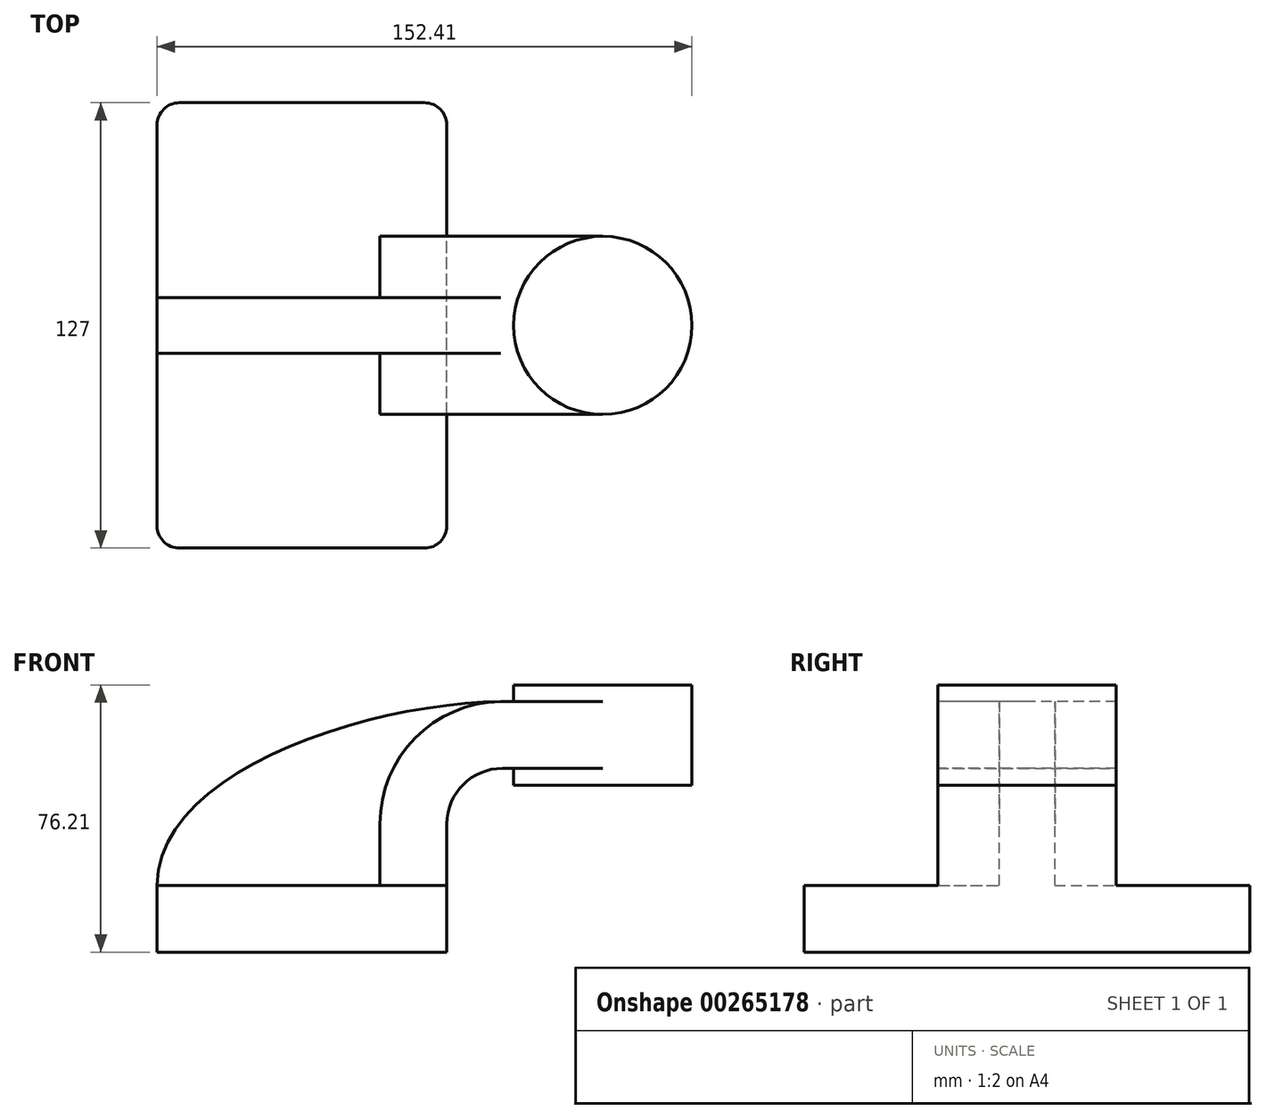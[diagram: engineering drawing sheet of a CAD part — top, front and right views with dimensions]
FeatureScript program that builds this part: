
annotation { "Feature Type Name" : "Feature", "Feature Type Description" : "" }
export const myFeature = defineFeature(function(context is Context, id is Id, definition is map)
    precondition{}
    {
        {
            var Q0;
            Q0=qCreatedBy(makeId("Front.planeOp"),FACE);
            var sketch = newSketch(context, id + "F0", { "sketchPlane" : qUnion([Q0])});
            skLineSegment(sketch, "E0.bottom", {"start": v(-41.28, 9.52) * mm, "end": v(41.28, 9.52) * mm});
            skLineSegment(sketch, "E0.top", {"start": v(-41.28, -9.53) * mm, "end": v(41.28, -9.53) * mm});
            skLineSegment(sketch, "E0.left", {"start": v(-41.28, 9.52) * mm, "end": v(-41.28, -9.53) * mm});
            skLineSegment(sketch, "E0.right", {"start": v(41.28, 9.52) * mm, "end": v(41.28, -9.53) * mm});
            skPoint(sketch, "E0.middle", {"position": v(0, 0) * mm});
            skLineSegment(sketch, "E1.bottom", {"start": v(60.33, 38.1) * mm, "end": v(111.13, 38.1) * mm});
            skLineSegment(sketch, "E1.top", {"start": v(60.33, 66.67) * mm, "end": v(111.13, 66.67) * mm});
            skLineSegment(sketch, "E1.left", {"start": v(60.33, 38.1) * mm, "end": v(60.33, 66.67) * mm});
            skLineSegment(sketch, "E1.right", {"start": v(111.13, 38.1) * mm, "end": v(111.13, 66.67) * mm});
            skPoint(sketch, "E1.middle", {"position": v(85.73, 52.39) * mm});
            skLineSegment(sketch, "E2", {"start": v(41.28, 9.52) * mm, "end": v(41.28, 27) * mm});
            skArc(sketch, "E3", {"start": v(41.28, 27) * mm, "mid": v(45.92, 38.23) * mm, "end": v(57.15, 42.88) * mm});
            skLineSegment(sketch, "E4", {"start": v(57.15, 42.88) * mm, "end": v(85.72, 42.88) * mm});
            skLineSegment(sketch, "E5.0", {"start": v(57.15, 61.93) * mm, "end": v(85.72, 61.93) * mm});
            skArc(sketch, "E5.1", {"start": v(22.23, 27) * mm, "mid": v(32.45, 51.7) * mm, "end": v(57.15, 61.93) * mm});
            skLineSegment(sketch, "E5.2", {"start": v(22.23, 9.52) * mm, "end": v(22.23, 27) * mm});
            skFitSpline(sketch, "E6", {"points": [v(-41.28, 9.53) * mm, v(57.15, 61.93) * mm], "startDerivative": vector(0.5, 99.63) * mm, "endDerivative": vector(110.98, 0.55) * mm});
            skLineSegment(sketch, "E7", {"start": v(85.73, 38.1) * mm, "end": v(85.73, 66.67) * mm});
            skSolve(sketch);
        }
        {
            var Q0;
            Q0=makeQuery(id+"F0.imprint","IMPRINT",FACE,{"disambiguationData":[TD([[makeQuery(id+"F0.imprint","IMPRINT",EDGE,{"derivedFrom":sQuery(id+"F0.wireOp",EDGE,"E0.top")}),1.0]])]});
            extrude(context, id + "F1", {"entities" : qUnion([Q0]), "endBound" : BoundingType.SYMMETRIC, "depth" : 127 * mm});
        }
        {
            var Q0;
            {var subQ0=sQuery(id+"F0.wireOp",EDGE,"E4");var subQ1=sQuery(id+"F0.wireOp",EDGE,"E1.left");var subQ2=makeQuery(id+"F0.imprint","INTERSECT",VERTEX,{"derivedFrom":[subQ1,subQ0]});Q0=makeQuery(id+"F0.imprint","IMPRINT",FACE,{"disambiguationData":[TD([[makeQuery(id+"F0.imprint","IMPRINT",EDGE,{"disambiguationData":[TD([[subQ2,-1.0]])],"derivedFrom":subQ1}),-1.0]])]});}
            var Q1;
            {var subQ1=sQuery(id+"F0.wireOp",EDGE,"E2");Q1=makeQuery(id+"F0.imprint","IMPRINT",FACE,{"disambiguationData":[TD([[makeQuery(id+"F0.imprint","IMPRINT",EDGE,{"derivedFrom":subQ1}),1.0]])]});}
            extrude(context, id + "F2", {"entities" : qUnion([Q0, Q1]), "operationType" : NewBodyOperationType.ADD, "endBound" : BoundingType.SYMMETRIC, "depth" : 50.8 * mm});
        }
        {
            var Q0;
            {var subQ3=sQuery(id+"F0.wireOp",EDGE,"E5.2");Q0=makeQuery(id+"F0.imprint","IMPRINT",FACE,{"disambiguationData":[TD([[makeQuery(id+"F0.imprint","IMPRINT",EDGE,{"derivedFrom":subQ3}),1.0]])]});}
            extrude(context, id + "F3", {"entities" : qUnion([Q0]), "operationType" : NewBodyOperationType.ADD, "endBound" : BoundingType.SYMMETRIC, "depth" : 15.88 * mm});
        }
        {
            var Q0;
            {var subQ0=sQuery(id+"F0.wireOp",EDGE,"E1.right");Q0=makeQuery(id+"F0.imprint","IMPRINT",FACE,{"disambiguationData":[TD([[makeQuery(id+"F0.imprint","IMPRINT",EDGE,{"derivedFrom":subQ0}),1.0]])]});}
            var Q1;
            Q1=sQuery(id+"F0.wireOp",EDGE,"E7");
            revolve(context, id + "F4", {"operationType" : NewBodyOperationType.ADD, "entities" : qUnion([Q0]), "axis" : qUnion([Q1]), "revolveType" : RevolveType.FULL});
        }
        {
            var Q0;
            Q0=makeQuery(id+"F1.opExtrude","CAP_EDGE",EDGE,{"disambiguationData":[OSD([sQuery(id+"F0.wireOp",EDGE,"E0.right")])],"isStart":false});
            var Q1;
            Q1=makeQuery(id+"F1.opExtrude","CAP_EDGE",EDGE,{"disambiguationData":[OSD([sQuery(id+"F0.wireOp",EDGE,"E0.left")])],"isStart":false});
            var Q2;
            Q2=makeQuery(id+"F1.opExtrude","CAP_EDGE",EDGE,{"disambiguationData":[OSD([sQuery(id+"F0.wireOp",EDGE,"E0.right")])],"isStart":true});
            var Q3;
            Q3=makeQuery(id+"F1.opExtrude","CAP_EDGE",EDGE,{"disambiguationData":[OSD([sQuery(id+"F0.wireOp",EDGE,"E0.left")])],"isStart":true});
            fillet(context, id + "F5", {"entities" : qUnion([Q0, Q1, Q2, Q3]), "radius" : 6.35 * mm, "tangentPropagation" : true, "allowEdgeOverflow" : false});
        }
    });
